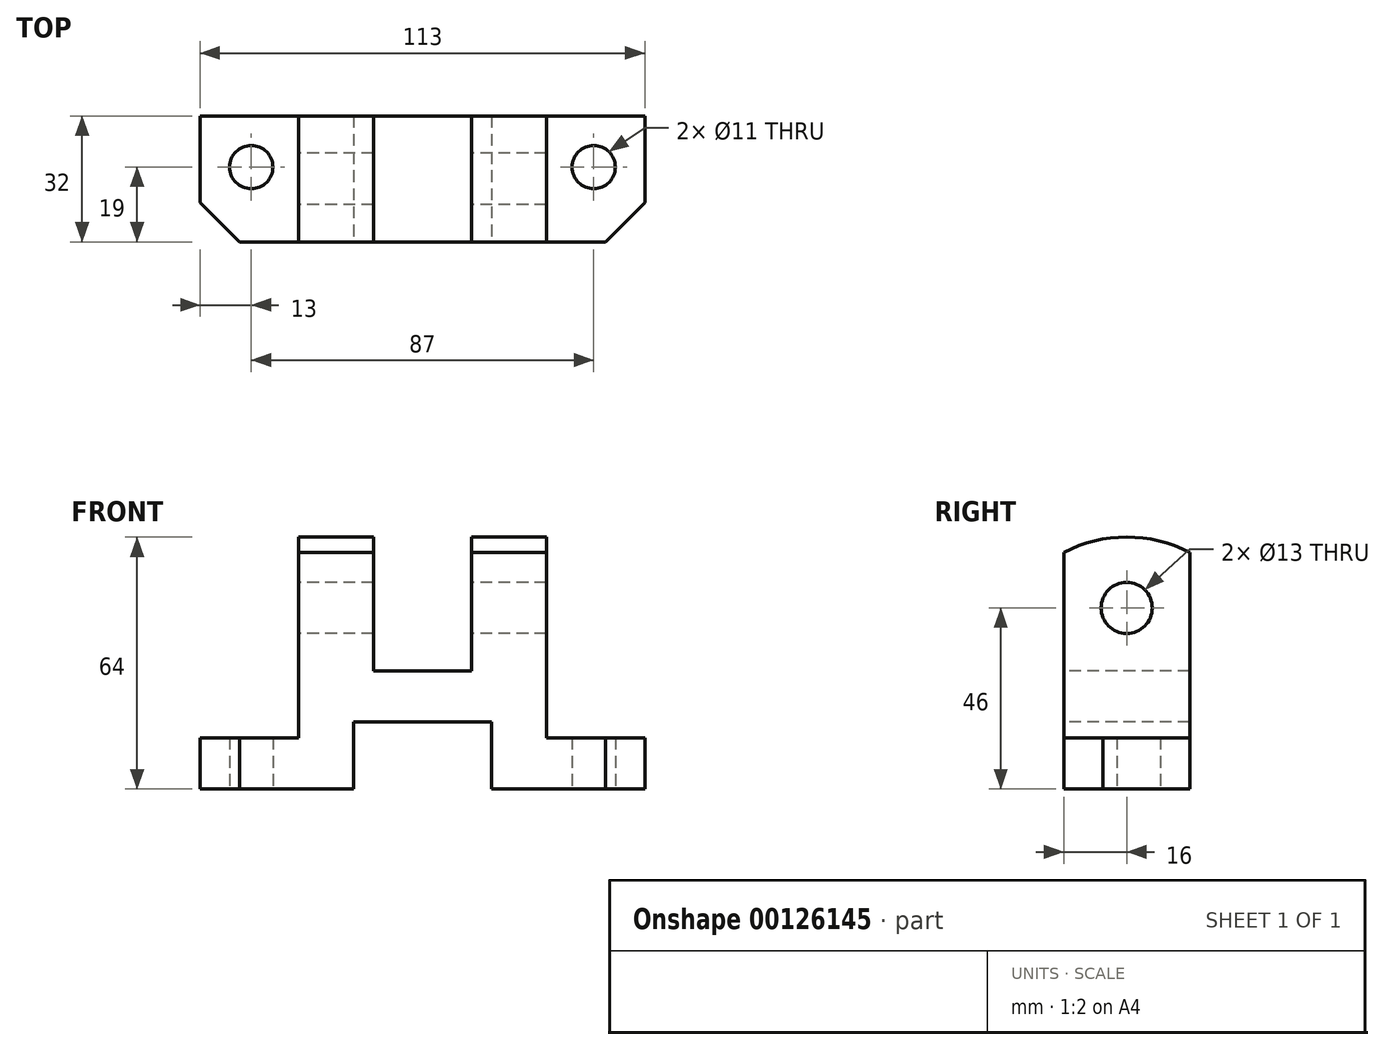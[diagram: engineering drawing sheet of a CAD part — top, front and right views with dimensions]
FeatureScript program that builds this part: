
annotation { "Feature Type Name" : "Feature", "Feature Type Description" : "" }
export const myFeature = defineFeature(function(context is Context, id is Id, definition is map)
    precondition{}
    {
        {
            var Q0;
            Q0=qCreatedBy(makeId("Right.planeOp"),FACE);
            var sketch = newSketch(context, id + "F0", { "sketchPlane" : qUnion([Q0])});
            skLineSegment(sketch, "E0", {"start": v(0, 0) * mm, "end": v(32, 0) * mm});
            skLineSegment(sketch, "E1", {"start": v(32, 0) * mm, "end": v(32, 60.13) * mm});
            skLineSegment(sketch, "E2", {"start": v(0, 0) * mm, "end": v(0, 60.13) * mm});
            skArc(sketch, "E3", {"start": v(32, 60.13) * mm, "mid": v(16, 64) * mm, "end": v(0, 60.13) * mm});
            skCircle(sketch, "E4", {"center": v(16, 46) * mm, "radius": 6.5 * mm});
            skSolve(sketch);
        }
        {
            var Q0;
            Q0 = qSketchRegion(id + "F0", true);
            extrude(context, id + "F1", {"entities" : qUnion([Q0]), "depth" : 113 * mm});
        }
        {
            var Q0;
            Q0=makeQuery(id+"F1.opExtrude","SWEPT_FACE",FACE,{"disambiguationData":[OSD([sQuery(id+"F0.wireOp",EDGE,"E2")])]});
            var sketch = newSketch(context, id + "F2", { "sketchPlane" : qUnion([Q0])});
            skLineSegment(sketch, "E5", {"start": v(0, 13) * mm, "end": v(25, 13) * mm});
            skLineSegment(sketch, "E6", {"start": v(25, 13) * mm, "end": v(25, 66.88) * mm});
            skLineSegment(sketch, "E7", {"start": v(113, 13) * mm, "end": v(88, 13) * mm});
            skLineSegment(sketch, "E8", {"start": v(88, 13) * mm, "end": v(88, 66.88) * mm});
            skLineSegment(sketch, "E9", {"start": v(74, 0) * mm, "end": v(74, 17) * mm});
            skLineSegment(sketch, "E10", {"start": v(74, 17) * mm, "end": v(39, 17) * mm});
            skLineSegment(sketch, "E11", {"start": v(39, 17) * mm, "end": v(39, 0) * mm});
            skLineSegment(sketch, "E12", {"start": v(44, 30) * mm, "end": v(69, 30) * mm});
            skLineSegment(sketch, "E13", {"start": v(69, 30) * mm, "end": v(69, 66.88) * mm});
            skLineSegment(sketch, "E14", {"start": v(44, 30) * mm, "end": v(44, 66.88) * mm});
            skLineSegment(sketch, "E15", {"start": v(0, 13) * mm, "end": v(0, 66.88) * mm});
            skLineSegment(sketch, "E16", {"start": v(0, 66.88) * mm, "end": v(25, 66.88) * mm});
            skLineSegment(sketch, "E17", {"start": v(113, 13) * mm, "end": v(113, 66.88) * mm});
            skLineSegment(sketch, "E18", {"start": v(113, 66.88) * mm, "end": v(88, 66.88) * mm});
            skLineSegment(sketch, "E19", {"start": v(69, 66.88) * mm, "end": v(44, 66.88) * mm});
            skSolve(sketch);
        }
        {
            var Q0;
            Q0 = qSketchRegion(id + "F2", true);
            var Q1;
            {var subQ0=sQuery(id+"F2.wireOp",EDGE,"E9");Q1=makeQuery(id+"F2.imprint","IMPRINT",FACE,{"disambiguationData":[TD([[makeQuery(id+"F2.imprint","IMPRINT",EDGE,{"derivedFrom":subQ0}),1.0]])]});}
            extrude(context, id + "F3", {"entities" : qUnion([Q0, Q1]), "operationType" : NewBodyOperationType.REMOVE, "endBound" : BoundingType.THROUGH_ALL, "oppositeDirection" : true, "depth" : 25 * mm});
        }
        {
            var Q0;
            {var subQ2=sQuery(id+"F0.wireOp",EDGE,"E0");Q0=makeQuery(id+"F3.boolean.opBoolean","SPLIT",FACE,{"disambiguationData":[TD([makeQuery(id+"F3.opExtrude","SWEPT_FACE",FACE,{"disambiguationData":[OSD([sQuery(id+"F2.wireOp",EDGE,"E9")])]})])],"derivedFrom":makeQuery(id+"F1.opExtrude","SWEPT_FACE",FACE,{"disambiguationData":[OSD([subQ2])]})});}
            var sketch = newSketch(context, id + "F4", { "sketchPlane" : qUnion([Q0])});
            skLineSegment(sketch, "E20", {"start": v(0, -10) * mm, "end": v(10, 0) * mm});
            skLineSegment(sketch, "E21", {"start": v(103, 0) * mm, "end": v(113, -10) * mm});
            skLineSegment(sketch, "E22", {"start": v(0, -19) * mm, "end": v(113, -19) * mm, "construction": true});
            skLineSegment(sketch, "E23", {"start": v(100, -32) * mm, "end": v(100, 0) * mm, "construction": true});
            skLineSegment(sketch, "E24", {"start": v(13, 0) * mm, "end": v(13, -32.08) * mm, "construction": true});
            skCircle(sketch, "E25", {"center": v(100, -19) * mm, "radius": 5.5 * mm});
            skCircle(sketch, "E26", {"center": v(13, -19) * mm, "radius": 5.5 * mm});
            skLineSegment(sketch, "E27", {"start": v(0, -10) * mm, "end": v(0, 0) * mm});
            skLineSegment(sketch, "E28", {"start": v(0, 0) * mm, "end": v(10, 0) * mm});
            skSolve(sketch);
        }
        {
            var Q0;
            Q0 = qSketchRegion(id + "F4", true);
            var Q1;
            {var subQ0=sQuery(id+"F4.wireOp",EDGE,"E21");Q1=makeQuery(id+"F4.imprint","IMPRINT",FACE,{"disambiguationData":[TD([[makeQuery(id+"F4.imprint","IMPRINT",EDGE,{"derivedFrom":subQ0}),1.0]])]});}
            extrude(context, id + "F5", {"entities" : qUnion([Q0, Q1]), "operationType" : NewBodyOperationType.REMOVE, "endBound" : BoundingType.THROUGH_ALL, "oppositeDirection" : true, "depth" : 25 * mm});
        }
    });
